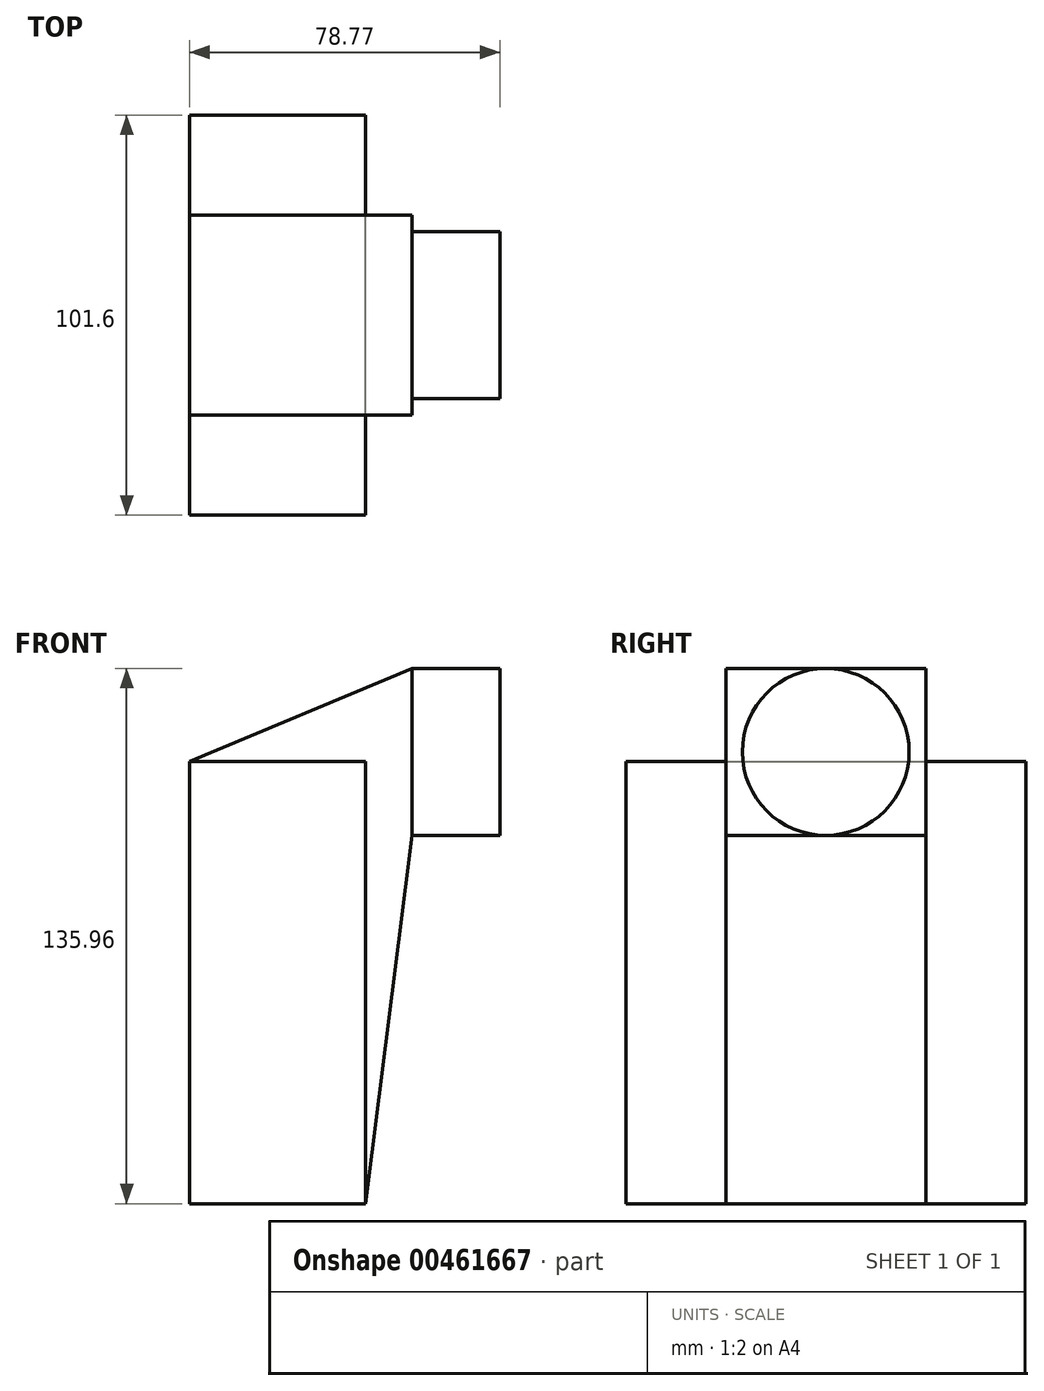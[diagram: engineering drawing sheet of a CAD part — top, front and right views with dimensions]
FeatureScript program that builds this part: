
annotation { "Feature Type Name" : "Feature", "Feature Type Description" : "" }
export const myFeature = defineFeature(function(context is Context, id is Id, definition is map)
    precondition{}
    {
        {
            var Q0;
            Q0=qCreatedBy(makeId("Front.planeOp"),FACE);
            var sketch = newSketch(context, id + "F0", { "sketchPlane" : qUnion([Q0])});
            skLineSegment(sketch, "E0.bottom", {"start": v(22.3, 56.19) * mm, "end": v(-22.3, 56.19) * mm});
            skLineSegment(sketch, "E0.top", {"start": v(22.3, -56.19) * mm, "end": v(-22.3, -56.19) * mm});
            skLineSegment(sketch, "E0.left", {"start": v(22.3, 56.19) * mm, "end": v(22.3, -56.19) * mm});
            skLineSegment(sketch, "E0.right", {"start": v(-22.3, 56.19) * mm, "end": v(-22.3, -56.19) * mm});
            skPoint(sketch, "E0.middle", {"position": v(0, 0) * mm});
            skLineSegment(sketch, "E1.bottom", {"start": v(34.22, 37.38) * mm, "end": v(56.47, 37.38) * mm});
            skLineSegment(sketch, "E1.top", {"start": v(34.22, 79.77) * mm, "end": v(56.47, 79.77) * mm});
            skLineSegment(sketch, "E1.left", {"start": v(34.22, 37.38) * mm, "end": v(34.22, 79.77) * mm});
            skLineSegment(sketch, "E1.right", {"start": v(56.47, 37.38) * mm, "end": v(56.47, 79.77) * mm});
            skPoint(sketch, "E1.middle", {"position": v(45.35, 58.57) * mm});
            skLineSegment(sketch, "E2", {"start": v(22.3, 56.19) * mm, "end": v(34.22, 79.77) * mm});
            skLineSegment(sketch, "E3", {"start": v(22.3, -56.19) * mm, "end": v(34.22, 37.38) * mm});
            skLineSegment(sketch, "E4", {"start": v(34.22, 58.57) * mm, "end": v(56.47, 58.57) * mm});
            skLineSegment(sketch, "E5", {"start": v(-22.3, 56.19) * mm, "end": v(34.22, 79.77) * mm});
            skSolve(sketch);
        }
        {
            var Q0;
            Q0=makeQuery(id+"F0.imprint","IMPRINT",FACE,{"disambiguationData":[TD([[makeQuery(id+"F0.imprint","IMPRINT",EDGE,{"derivedFrom":sQuery(id+"F0.wireOp",EDGE,"E0.bottom")}),1.0]])]});
            extrude(context, id + "F1", {"entities" : qUnion([Q0]), "endBound" : BoundingType.SYMMETRIC, "depth" : 101.6 * mm});
        }
        {
            var Q0;
            {var subQ0=sQuery(id+"F0.wireOp",EDGE,"E1.top");Q0=makeQuery(id+"F0.imprint","IMPRINT",FACE,{"disambiguationData":[TD([[makeQuery(id+"F0.imprint","IMPRINT",EDGE,{"derivedFrom":subQ0}),-1.0]])]});}
            var Q1;
            Q1=sQuery(id+"F0.wireOp",EDGE,"E4");
            revolve(context, id + "F2", {"entities" : qUnion([Q0]), "axis" : qUnion([Q1]), "revolveType" : RevolveType.FULL});
        }
        {
            var Q0;
            Q0=makeQuery(id+"F0.imprint","IMPRINT",FACE,{"disambiguationData":[TD([[makeQuery(id+"F0.imprint","IMPRINT",EDGE,{"derivedFrom":sQuery(id+"F0.wireOp",EDGE,"E0.left")}),1.0]])]});
            var Q1;
            Q1=makeQuery(id+"F0.imprint","IMPRINT",FACE,{"disambiguationData":[TD([[makeQuery(id+"F0.imprint","IMPRINT",EDGE,{"derivedFrom":sQuery(id+"F0.wireOp",EDGE,"E0.bottom")}),-1.0]])]});
            extrude(context, id + "F3", {"entities" : qUnion([Q0, Q1]), "endBound" : BoundingType.SYMMETRIC, "depth" : 50.8 * mm});
        }
    });
